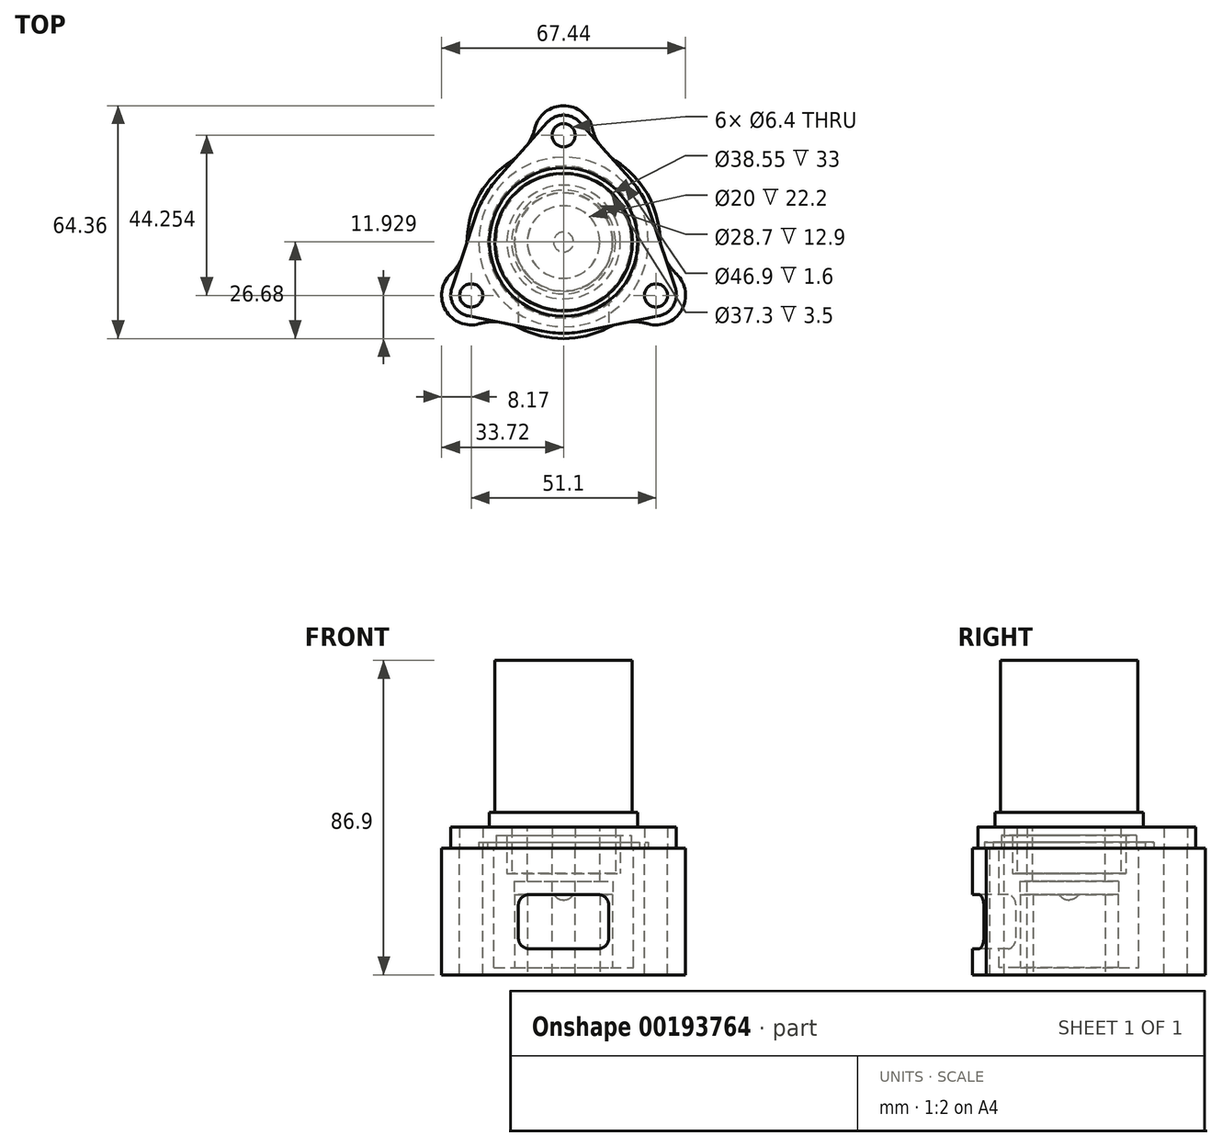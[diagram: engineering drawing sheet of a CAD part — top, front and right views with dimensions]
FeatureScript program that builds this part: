
annotation { "Feature Type Name" : "Feature", "Feature Type Description" : "" }
export const myFeature = defineFeature(function(context is Context, id is Id, definition is map)
    precondition{}
    {
        {
            var Q0;
            Q0=qCreatedBy(makeId("Top.planeOp"),FACE);
            var sketch = newSketch(context, id + "F0", { "sketchPlane" : qUnion([Q0])});
            skCircle(sketch, "E0", {"center": v(0, 29.5) * mm, "radius": 3.2 * mm});
            skCircle(sketch, "E1", {"center": v(25.55, -14.75) * mm, "radius": 3.2 * mm});
            skCircle(sketch, "E2", {"center": v(-25.55, -14.75) * mm, "radius": 3.2 * mm});
            skCircle(sketch, "E3", {"center": v(0, 0) * mm, "radius": 14.35 * mm});
            skLineSegment(sketch, "E4", {"start": v(0, 29.5) * mm, "end": v(25.55, -14.75) * mm, "construction": true});
            skLineSegment(sketch, "E5", {"start": v(-25.55, -14.75) * mm, "end": v(25.55, -14.75) * mm, "construction": true});
            skLineSegment(sketch, "E6", {"start": v(0, 29.5) * mm, "end": v(-25.55, -14.75) * mm, "construction": true});
            skLineSegment(sketch, "E7", {"start": v(-22.39, 12.93) * mm, "end": v(0, 38.1) * mm});
            skLineSegment(sketch, "E8", {"start": v(0, 38.1) * mm, "end": v(22.39, 12.92) * mm});
            skLineSegment(sketch, "E9", {"start": v(22.39, 12.92) * mm, "end": v(33, -19.05) * mm});
            skLineSegment(sketch, "E10", {"start": v(33, -19.05) * mm, "end": v(0, -25.85) * mm});
            skLineSegment(sketch, "E11", {"start": v(0, -25.85) * mm, "end": v(-33, -19.05) * mm});
            skLineSegment(sketch, "E12", {"start": v(-33, -19.05) * mm, "end": v(-22.39, 12.93) * mm});
            skLineSegment(sketch, "E13", {"start": v(0, 38.1) * mm, "end": v(-33, -19.05) * mm, "construction": true});
            skLineSegment(sketch, "E14", {"start": v(0, 38.1) * mm, "end": v(33, -19.05) * mm, "construction": true});
            skLineSegment(sketch, "E15", {"start": v(33, -19.05) * mm, "end": v(-33, -19.05) * mm, "construction": true});
            skLineSegment(sketch, "E16", {"start": v(0, 29.5) * mm, "end": v(0, 38.1) * mm, "construction": true});
            skLineSegment(sketch, "E17", {"start": v(-25.55, -14.75) * mm, "end": v(-33, -19.05) * mm, "construction": true});
            skLineSegment(sketch, "E18", {"start": v(25.55, -14.75) * mm, "end": v(33, -19.05) * mm, "construction": true});
            skLineSegment(sketch, "E19", {"start": v(0, 29.5) * mm, "end": v(0, 0) * mm, "construction": true});
            skLineSegment(sketch, "E20", {"start": v(0, 0) * mm, "end": v(-25.55, -14.75) * mm, "construction": true});
            skLineSegment(sketch, "E21", {"start": v(0, 0) * mm, "end": v(25.55, -14.75) * mm, "construction": true});
            skSolve(sketch);
        }
        {
            var Q0;
            Q0 = qSketchRegion(id + "F0", true);
            extrude(context, id + "F1", {"entities" : qUnion([Q0]), "depth" : 5.9 * mm});
        }
        {
            var Q0;
            Q0=makeQuery(id+"F1.opExtrude","SWEPT_EDGE",EDGE,{"disambiguationData":[OSD([sQuery(id+"F0.wireOp",EDGE,"E11"),sQuery(id+"F0.wireOp",EDGE,"E12")])]});
            var Q1;
            Q1=makeQuery(id+"F1.opExtrude","SWEPT_EDGE",EDGE,{"disambiguationData":[OSD([sQuery(id+"F0.wireOp",EDGE,"E9"),sQuery(id+"F0.wireOp",EDGE,"E10")])]});
            var Q2;
            Q2=makeQuery(id+"F1.opExtrude","SWEPT_EDGE",EDGE,{"disambiguationData":[OSD([sQuery(id+"F0.wireOp",EDGE,"E7"),sQuery(id+"F0.wireOp",EDGE,"E8")])]});
            fillet(context, id + "F2", {"entities" : qUnion([Q0, Q1, Q2]), "radius" : 6 * mm, "tangentPropagation" : true, "allowEdgeOverflow" : false});
        }
        {
            var Q0;
            Q0=makeQuery(id+"F1.opExtrude","SWEPT_EDGE",EDGE,{"disambiguationData":[OSD([sQuery(id+"F0.wireOp",EDGE,"E7"),sQuery(id+"F0.wireOp",EDGE,"E12")])]});
            var Q1;
            Q1=makeQuery(id+"F1.opExtrude","SWEPT_EDGE",EDGE,{"disambiguationData":[OSD([sQuery(id+"F0.wireOp",EDGE,"E8"),sQuery(id+"F0.wireOp",EDGE,"E9")])]});
            var Q2;
            Q2=makeQuery(id+"F1.opExtrude","SWEPT_EDGE",EDGE,{"disambiguationData":[OSD([sQuery(id+"F0.wireOp",EDGE,"E10"),sQuery(id+"F0.wireOp",EDGE,"E11")])]});
            fillet(context, id + "F3", {"entities" : qUnion([Q0, Q1, Q2]), "radius" : 30 * mm, "tangentPropagation" : true, "allowEdgeOverflow" : false});
        }
        {
            var Q0;
            Q0=makeQuery(id+"F1.opExtrude","CAP_FACE",FACE,{"disambiguationData":[OSD([sQuery(id+"F0.wireOp",EDGE,"E0"),sQuery(id+"F0.wireOp",EDGE,"E1"),sQuery(id+"F0.wireOp",EDGE,"E2"),sQuery(id+"F0.wireOp",EDGE,"E3"),sQuery(id+"F0.wireOp",EDGE,"E7"),sQuery(id+"F0.wireOp",EDGE,"E8"),sQuery(id+"F0.wireOp",EDGE,"E9"),sQuery(id+"F0.wireOp",EDGE,"E10"),sQuery(id+"F0.wireOp",EDGE,"E11"),sQuery(id+"F0.wireOp",EDGE,"E12")])],"isStart":true});
            var sketch = newSketch(context, id + "F4", { "sketchPlane" : qUnion([Q0])});
            skCircle(sketch, "E22", {"center": v(0, 0) * mm, "radius": 23.45 * mm});
            skCircle(sketch, "E23", {"center": v(0, 0) * mm, "radius": 21 * mm});
            skSolve(sketch);
        }
        {
            var Q0;
            Q0 = qSketchRegion(id + "F4", true);
            extrude(context, id + "F5", {"entities" : qUnion([Q0]), "operationType" : NewBodyOperationType.REMOVE, "oppositeDirection" : true, "depth" : 1.6 * mm});
        }
        {
            var Q0;
            {var subQ0=sQuery(id+"F0.wireOp",EDGE,"E3");Q0=makeQuery(id+"F5.boolean.opBoolean","SPLIT",FACE,{"disambiguationData":[TD([makeQuery(id+"F1.opExtrude","SWEPT_FACE",FACE,{"disambiguationData":[OSD([subQ0])]})])],"derivedFrom":makeQuery(id+"F1.opExtrude","CAP_FACE",FACE,{"disambiguationData":[OSD([sQuery(id+"F0.wireOp",EDGE,"E0"),sQuery(id+"F0.wireOp",EDGE,"E1"),sQuery(id+"F0.wireOp",EDGE,"E2"),subQ0,sQuery(id+"F0.wireOp",EDGE,"E7"),sQuery(id+"F0.wireOp",EDGE,"E8"),sQuery(id+"F0.wireOp",EDGE,"E9"),sQuery(id+"F0.wireOp",EDGE,"E10"),sQuery(id+"F0.wireOp",EDGE,"E11"),sQuery(id+"F0.wireOp",EDGE,"E12")])],"isStart":true})});}
            var sketch = newSketch(context, id + "F6", { "sketchPlane" : qUnion([Q0])});
            skCircle(sketch, "E24", {"center": v(0, 0) * mm, "radius": 18.65 * mm});
            skCircle(sketch, "E25", {"center": v(0, 0) * mm, "radius": 15.7 * mm});
            skSolve(sketch);
        }
        {
            var Q0;
            Q0 = qSketchRegion(id + "F6", true);
            extrude(context, id + "F7", {"entities" : qUnion([Q0]), "operationType" : NewBodyOperationType.REMOVE, "oppositeDirection" : true, "depth" : 3.5 * mm});
        }
        {
            var Q0;
            {var subQ0=sQuery(id+"F0.wireOp",EDGE,"E3");var subQ1=makeQuery(id+"F1.opExtrude","SWEPT_FACE",FACE,{"disambiguationData":[OSD([subQ0])]});Q0=makeQuery(id+"F7.boolean.opBoolean","SPLIT",FACE,{"disambiguationData":[TD([subQ1])],"derivedFrom":makeQuery(id+"F5.boolean.opBoolean","SPLIT",FACE,{"disambiguationData":[TD([subQ1])],"derivedFrom":makeQuery(id+"F1.opExtrude","CAP_FACE",FACE,{"disambiguationData":[OSD([sQuery(id+"F0.wireOp",EDGE,"E0"),sQuery(id+"F0.wireOp",EDGE,"E1"),sQuery(id+"F0.wireOp",EDGE,"E2"),subQ0,sQuery(id+"F0.wireOp",EDGE,"E7"),sQuery(id+"F0.wireOp",EDGE,"E8"),sQuery(id+"F0.wireOp",EDGE,"E9"),sQuery(id+"F0.wireOp",EDGE,"E10"),sQuery(id+"F0.wireOp",EDGE,"E11"),sQuery(id+"F0.wireOp",EDGE,"E12")])],"isStart":true})})});}
            extrude(context, id + "F8", {"entities" : qUnion([Q0]), "operationType" : NewBodyOperationType.ADD, "depth" : 7 * mm});
        }
        {
            var Q0;
            Q0=qCreatedBy(makeId("Front.planeOp"),FACE);
            var sketch = newSketch(context, id + "F9", { "sketchPlane" : qUnion([Q0])});
            skLineSegment(sketch, "E26", {"start": v(0, 5.9) * mm, "end": v(20.5, 5.9) * mm});
            skLineSegment(sketch, "E27", {"start": v(20.5, 5.9) * mm, "end": v(20.5, 9.9) * mm});
            skLineSegment(sketch, "E28", {"start": v(20.5, 9.9) * mm, "end": v(19, 9.9) * mm});
            skLineSegment(sketch, "E29", {"start": v(19, 9.9) * mm, "end": v(19, 51.9) * mm});
            skLineSegment(sketch, "E30", {"start": v(19, 51.9) * mm, "end": v(0, 51.9) * mm});
            skLineSegment(sketch, "E31", {"start": v(0, 51.9) * mm, "end": v(0, 5.9) * mm});
            skSolve(sketch);
        }
        {
            var Q0;
            Q0 = qSketchRegion(id + "F9", true);
            var Q1;
            Q1=sQuery(id+"F9.wireOp",EDGE,"E31");
            revolve(context, id + "F10", {"operationType" : NewBodyOperationType.ADD, "entities" : qUnion([Q0]), "axis" : qUnion([Q1]), "revolveType" : RevolveType.FULL});
        }
        {
            var Q0;
            Q0=makeQuery(id+"F10.opRevolve","SWEPT_FACE",FACE,{"disambiguationData":[OSD([sQuery(id+"F9.wireOp",EDGE,"E26")])]});
            var sketch = newSketch(context, id + "F11", { "sketchPlane" : qUnion([Q0])});
            skCircle(sketch, "E32", {"center": v(0, 0) * mm, "radius": 10.05 * mm});
            skSolve(sketch);
        }
        {
            var Q0;
            Q0 = qSketchRegion(id + "F11", true);
            var Q1;
            Q1=makeQuery(id+"F8.opExtrude","CAP_FACE",FACE,{"disambiguationData":[OSD([sQuery(id+"F0.wireOp",EDGE,"E0"),sQuery(id+"F0.wireOp",EDGE,"E1"),sQuery(id+"F0.wireOp",EDGE,"E2"),sQuery(id+"F0.wireOp",EDGE,"E3"),sQuery(id+"F0.wireOp",EDGE,"E7"),sQuery(id+"F0.wireOp",EDGE,"E8"),sQuery(id+"F0.wireOp",EDGE,"E9"),sQuery(id+"F0.wireOp",EDGE,"E10"),sQuery(id+"F0.wireOp",EDGE,"E11"),sQuery(id+"F0.wireOp",EDGE,"E12")])],"isStart":false});
            extrude(context, id + "F12", {"entities" : qUnion([Q0]), "endBoundEntityFace" : qUnion([Q1]), "depth" : 18.7 * mm});
        }
        {
            var Q0;
            Q0=makeQuery(id+"F12.opExtrude","CAP_FACE",FACE,{"disambiguationData":[OSD([sQuery(id+"F11.wireOp",EDGE,"E32")])],"isStart":false});
            var sketch = newSketch(context, id + "F13", { "sketchPlane" : qUnion([Q0])});
            skCircle(sketch, "E33", {"center": v(0, 0) * mm, "radius": 13.65 * mm});
            skSolve(sketch);
        }
        {
            var Q0;
            Q0 = qSketchRegion(id + "F13", true);
            extrude(context, id + "F14", {"entities" : qUnion([Q0]), "operationType" : NewBodyOperationType.ADD, "oppositeDirection" : true, "depth" : 3.7 * mm});
        }
        {
            var Q0;
            Q0=qCreatedBy(makeId("Front.planeOp"),FACE);
            var sketch = newSketch(context, id + "F15", { "sketchPlane" : qUnion([Q0])});
            skLineSegment(sketch, "E34", {"start": v(0, -9.1) * mm, "end": v(6.1, -9.1) * mm});
            skLineSegment(sketch, "E35", {"start": v(1.4, -14.3) * mm, "end": v(0, -14.3) * mm});
            skLineSegment(sketch, "E36", {"start": v(0, -14.3) * mm, "end": v(0, -9.1) * mm});
            skLineSegment(sketch, "E37", {"start": v(1.4, -14.3) * mm, "end": v(6.1, -9.1) * mm});
            skSolve(sketch);
        }
        {
            var Q0;
            Q0 = qSketchRegion(id + "F15", true);
            var Q1;
            Q1=sQuery(id+"F15.wireOp",EDGE,"E36");
            revolve(context, id + "F16", {"operationType" : NewBodyOperationType.ADD, "entities" : qUnion([Q0]), "axis" : qUnion([Q1]), "revolveType" : RevolveType.FULL});
        }
        {
            var Q0;
            Q0=makeQuery(id+"F16.opRevolve","SWEPT_EDGE",EDGE,{"disambiguationData":[OSD([sQuery(id+"F15.wireOp",EDGE,"E35"),sQuery(id+"F15.wireOp",EDGE,"E37")])]});
            var Q1;
            Q1=makeQuery(id+"F16.opRevolve","SWEPT_EDGE",EDGE,{"disambiguationData":[OSD([sQuery(id+"F15.wireOp",EDGE,"E34"),sQuery(id+"F15.wireOp",EDGE,"E37")])]});
            fillet(context, id + "F17", {"entities" : qUnion([Q0, Q1]), "radius" : 3 * mm, "tangentPropagation" : true, "allowEdgeOverflow" : false});
        }
        {
            var Q0;
            Q0=qCreatedBy(makeId("Top.planeOp"),FACE);
            var sketch = newSketch(context, id + "F18", { "sketchPlane" : qUnion([Q0])});
            skCircle(sketch, "E38", {"center": v(0, 0) * mm, "radius": 19.28 * mm});
            skArc(sketch, "E39", {"start": v(-18.63, -19.1) * mm, "mid": v(0, -26.68) * mm, "end": v(18.63, -19.1) * mm});
            skCircle(sketch, "E40", {"center": v(0, 29.5) * mm, "radius": 3.2 * mm});
            skCircle(sketch, "E41", {"center": v(-25.55, -14.75) * mm, "radius": 3.2 * mm});
            skCircle(sketch, "E42", {"center": v(25.55, -14.75) * mm, "radius": 3.2 * mm});
            skArc(sketch, "E43", {"start": v(-25.85, -6.58) * mm, "mid": v(-32.63, -18.84) * mm, "end": v(-18.63, -19.1) * mm});
            skArc(sketch, "E44", {"start": v(18.63, -19.1) * mm, "mid": v(32.63, -18.84) * mm, "end": v(25.85, -6.58) * mm});
            skArc(sketch, "E45", {"start": v(7.22, 25.68) * mm, "mid": v(0, 37.67) * mm, "end": v(-7.22, 25.68) * mm});
            skArc(sketch, "E46.trimOffspring", {"start": v(-7.22, 25.68) * mm, "mid": v(-23.1, 13.34) * mm, "end": v(-25.85, -6.58) * mm});
            skArc(sketch, "E47.trimOffspring", {"start": v(25.85, -6.58) * mm, "mid": v(23.1, 13.34) * mm, "end": v(7.22, 25.68) * mm});
            skSolve(sketch);
        }
        {
            var Q0;
            Q0 = qSketchRegion(id + "F18", true);
            extrude(context, id + "F19", {"entities" : qUnion([Q0]), "oppositeDirection" : true, "depth" : 35 * mm});
        }
        {
            var Q0;
            Q0=makeQuery(id+"F19.opExtrude","SWEPT_EDGE",EDGE,{"disambiguationData":[OSD([sQuery(id+"F18.wireOp",EDGE,"E43"),sQuery(id+"F18.wireOp",EDGE,"E46.trimOffspring")])]});
            var Q1;
            Q1=makeQuery(id+"F19.opExtrude","SWEPT_EDGE",EDGE,{"disambiguationData":[OSD([sQuery(id+"F18.wireOp",EDGE,"E45"),sQuery(id+"F18.wireOp",EDGE,"E46.trimOffspring")])]});
            var Q2;
            Q2=makeQuery(id+"F19.opExtrude","SWEPT_EDGE",EDGE,{"disambiguationData":[OSD([sQuery(id+"F18.wireOp",EDGE,"E45"),sQuery(id+"F18.wireOp",EDGE,"E47.trimOffspring")])]});
            var Q3;
            Q3=makeQuery(id+"F19.opExtrude","SWEPT_EDGE",EDGE,{"disambiguationData":[OSD([sQuery(id+"F18.wireOp",EDGE,"E44"),sQuery(id+"F18.wireOp",EDGE,"E47.trimOffspring")])]});
            var Q4;
            Q4=makeQuery(id+"F19.opExtrude","SWEPT_EDGE",EDGE,{"disambiguationData":[OSD([sQuery(id+"F18.wireOp",EDGE,"E39"),sQuery(id+"F18.wireOp",EDGE,"E44")])]});
            var Q5;
            Q5=makeQuery(id+"F19.opExtrude","SWEPT_EDGE",EDGE,{"disambiguationData":[OSD([sQuery(id+"F18.wireOp",EDGE,"E39"),sQuery(id+"F18.wireOp",EDGE,"E43")])]});
            fillet(context, id + "F20", {"entities" : qUnion([Q0, Q1, Q2, Q3, Q4, Q5]), "radius" : 15 * mm, "tangentPropagation" : true, "allowEdgeOverflow" : false});
        }
        {
            var Q0;
            Q0=makeQuery(id+"F19.opExtrude","CAP_FACE",FACE,{"disambiguationData":[OSD([sQuery(id+"F18.wireOp",EDGE,"E38"),sQuery(id+"F18.wireOp",EDGE,"E39"),sQuery(id+"F18.wireOp",EDGE,"E40"),sQuery(id+"F18.wireOp",EDGE,"E41"),sQuery(id+"F18.wireOp",EDGE,"E42"),sQuery(id+"F18.wireOp",EDGE,"E43"),sQuery(id+"F18.wireOp",EDGE,"E44"),sQuery(id+"F18.wireOp",EDGE,"E45"),sQuery(id+"F18.wireOp",EDGE,"E46.trimOffspring"),sQuery(id+"F18.wireOp",EDGE,"E47.trimOffspring")])],"isStart":false});
            var sketch = newSketch(context, id + "F21", { "sketchPlane" : qUnion([Q0])});
            skCircle(sketch, "E48", {"center": v(0, 0) * mm, "radius": 20 * mm});
            skCircle(sketch, "E49", {"center": v(0, 0) * mm, "radius": 10 * mm});
            skSolve(sketch);
        }
        {
            var Q0;
            Q0 = qSketchRegion(id + "F21", true);
            extrude(context, id + "F22", {"entities" : qUnion([Q0]), "operationType" : NewBodyOperationType.ADD, "oppositeDirection" : true, "depth" : 2 * mm});
        }
        {
            var Q0;
            Q0=makeQuery(id+"F22.opExtrude","CAP_FACE",FACE,{"disambiguationData":[OSD([sQuery(id+"F21.wireOp",EDGE,"E48")])],"isStart":false});
            var sketch = newSketch(context, id + "F23", { "sketchPlane" : qUnion([Q0])});
            skCircle(sketch, "E50", {"center": v(0, 0) * mm, "radius": 13.5 * mm});
            skCircle(sketch, "E51", {"center": v(0, 0) * mm, "radius": 10 * mm});
            skSolve(sketch);
        }
        {
            var Q0;
            Q0 = qSketchRegion(id + "F23", true);
            extrude(context, id + "F24", {"entities" : qUnion([Q0]), "operationType" : NewBodyOperationType.ADD, "depth" : (33 - 12.8) * mm});
        }
        {
            var Q0;
            {var subQ0=sQuery(id+"F18.wireOp",EDGE,"E39");var subQ1=sQuery(id+"F18.wireOp",EDGE,"E43");Q0=makeQuery(id+"F20.opFillet","BLEND_VERTEX",VERTEX,{"blendedFrom":[makeQuery(id+"F19.opExtrude","SWEPT_EDGE",EDGE,{"disambiguationData":[OSD([subQ0,subQ1])]}),makeQuery(id+"F19.opExtrude","CAP_FACE",FACE,{"disambiguationData":[OSD([sQuery(id+"F18.wireOp",EDGE,"E38"),subQ0,sQuery(id+"F18.wireOp",EDGE,"E40"),sQuery(id+"F18.wireOp",EDGE,"E41"),sQuery(id+"F18.wireOp",EDGE,"E42"),subQ1,sQuery(id+"F18.wireOp",EDGE,"E44"),sQuery(id+"F18.wireOp",EDGE,"E45"),sQuery(id+"F18.wireOp",EDGE,"E46.trimOffspring"),sQuery(id+"F18.wireOp",EDGE,"E47.trimOffspring")])],"isStart":true}),makeQuery(id+"F19.opExtrude","SWEPT_FACE",FACE,{"disambiguationData":[OSD([subQ0])]})],"blendedInto":[makeQuery(id+"F19.opExtrude","CAP_FACE",FACE,{"disambiguationData":[OSD([sQuery(id+"F18.wireOp",EDGE,"E38"),subQ0,sQuery(id+"F18.wireOp",EDGE,"E40"),sQuery(id+"F18.wireOp",EDGE,"E41"),sQuery(id+"F18.wireOp",EDGE,"E42"),subQ1,sQuery(id+"F18.wireOp",EDGE,"E44"),sQuery(id+"F18.wireOp",EDGE,"E45"),sQuery(id+"F18.wireOp",EDGE,"E46.trimOffspring"),sQuery(id+"F18.wireOp",EDGE,"E47.trimOffspring")])],"isStart":true}),makeQuery(id+"F19.opExtrude","SWEPT_FACE",FACE,{"disambiguationData":[OSD([subQ0])]})]});}
            var Q1;
            {var subQ0=sQuery(id+"F18.wireOp",EDGE,"E39");var subQ1=sQuery(id+"F18.wireOp",EDGE,"E43");Q1=makeQuery(id+"F20.opFillet","BLEND_VERTEX",VERTEX,{"blendedFrom":[makeQuery(id+"F19.opExtrude","SWEPT_EDGE",EDGE,{"disambiguationData":[OSD([subQ0,subQ1])]}),makeQuery(id+"F19.opExtrude","CAP_FACE",FACE,{"disambiguationData":[OSD([sQuery(id+"F18.wireOp",EDGE,"E38"),subQ0,sQuery(id+"F18.wireOp",EDGE,"E40"),sQuery(id+"F18.wireOp",EDGE,"E41"),sQuery(id+"F18.wireOp",EDGE,"E42"),subQ1,sQuery(id+"F18.wireOp",EDGE,"E44"),sQuery(id+"F18.wireOp",EDGE,"E45"),sQuery(id+"F18.wireOp",EDGE,"E46.trimOffspring"),sQuery(id+"F18.wireOp",EDGE,"E47.trimOffspring")])],"isStart":false}),makeQuery(id+"F19.opExtrude","SWEPT_FACE",FACE,{"disambiguationData":[OSD([subQ0])]})],"blendedInto":[makeQuery(id+"F19.opExtrude","CAP_FACE",FACE,{"disambiguationData":[OSD([sQuery(id+"F18.wireOp",EDGE,"E38"),subQ0,sQuery(id+"F18.wireOp",EDGE,"E40"),sQuery(id+"F18.wireOp",EDGE,"E41"),sQuery(id+"F18.wireOp",EDGE,"E42"),subQ1,sQuery(id+"F18.wireOp",EDGE,"E44"),sQuery(id+"F18.wireOp",EDGE,"E45"),sQuery(id+"F18.wireOp",EDGE,"E46.trimOffspring"),sQuery(id+"F18.wireOp",EDGE,"E47.trimOffspring")])],"isStart":false}),makeQuery(id+"F19.opExtrude","SWEPT_FACE",FACE,{"disambiguationData":[OSD([subQ0])]})]});}
            var Q2;
            {var subQ0=sQuery(id+"F18.wireOp",EDGE,"E39");var subQ1=sQuery(id+"F18.wireOp",EDGE,"E44");Q2=makeQuery(id+"F20.opFillet","BLEND_VERTEX",VERTEX,{"blendedFrom":[makeQuery(id+"F19.opExtrude","SWEPT_EDGE",EDGE,{"disambiguationData":[OSD([subQ0,subQ1])]}),makeQuery(id+"F19.opExtrude","CAP_FACE",FACE,{"disambiguationData":[OSD([sQuery(id+"F18.wireOp",EDGE,"E38"),subQ0,sQuery(id+"F18.wireOp",EDGE,"E40"),sQuery(id+"F18.wireOp",EDGE,"E41"),sQuery(id+"F18.wireOp",EDGE,"E42"),sQuery(id+"F18.wireOp",EDGE,"E43"),subQ1,sQuery(id+"F18.wireOp",EDGE,"E45"),sQuery(id+"F18.wireOp",EDGE,"E46.trimOffspring"),sQuery(id+"F18.wireOp",EDGE,"E47.trimOffspring")])],"isStart":false}),makeQuery(id+"F19.opExtrude","SWEPT_FACE",FACE,{"disambiguationData":[OSD([subQ0])]})],"blendedInto":[makeQuery(id+"F19.opExtrude","CAP_FACE",FACE,{"disambiguationData":[OSD([sQuery(id+"F18.wireOp",EDGE,"E38"),subQ0,sQuery(id+"F18.wireOp",EDGE,"E40"),sQuery(id+"F18.wireOp",EDGE,"E41"),sQuery(id+"F18.wireOp",EDGE,"E42"),sQuery(id+"F18.wireOp",EDGE,"E43"),subQ1,sQuery(id+"F18.wireOp",EDGE,"E45"),sQuery(id+"F18.wireOp",EDGE,"E46.trimOffspring"),sQuery(id+"F18.wireOp",EDGE,"E47.trimOffspring")])],"isStart":false}),makeQuery(id+"F19.opExtrude","SWEPT_FACE",FACE,{"disambiguationData":[OSD([subQ0])]})]});}
            cPlane(context, id + "F25", {"entities" : qUnion([Q0, Q1, Q2]), "cplaneType" : CPlaneType.THREE_POINT, "offset" : 25 * mm, "width" : 150 * mm, "height" : 150 * mm});
        }
        {
            var Q0;
            Q0=qCreatedBy(id+"F25.planeOp",FACE);
            var sketch = newSketch(context, id + "F26", { "sketchPlane" : qUnion([Q0])});
            skLineSegment(sketch, "E52.bottom", {"start": v(12.5, -12.8) * mm, "end": v(-12.5, -12.8) * mm});
            skLineSegment(sketch, "E52.top", {"start": v(12.5, -27.8) * mm, "end": v(-12.5, -27.8) * mm});
            skLineSegment(sketch, "E52.left", {"start": v(12.5, -12.8) * mm, "end": v(12.5, -27.8) * mm});
            skLineSegment(sketch, "E52.right", {"start": v(-12.5, -12.8) * mm, "end": v(-12.5, -27.8) * mm});
            skPoint(sketch, "E53", {"position": v(0, -12.8) * mm});
            skSolve(sketch);
        }
        {
            var Q0;
            Q0 = qSketchRegion(id + "F26", true);
            extrude(context, id + "F27", {"entities" : qUnion([Q0]), "operationType" : NewBodyOperationType.REMOVE, "depth" : 10 * mm, "hasSecondDirection" : true, "secondDirectionOppositeDirection" : true, "secondDirectionDepth" : 5 * mm});
        }
        {
            var Q0;
            Q0=makeQuery(id+"F27.boolean.opBoolean","COPY",EDGE,{"derivedFrom":makeQuery(id+"F27.opExtrude","SWEPT_EDGE",EDGE,{"disambiguationData":[OSD([sQuery(id+"F26.wireOp",EDGE,"E52.bottom"),sQuery(id+"F26.wireOp",EDGE,"E52.left")])]})});
            var Q1;
            Q1=makeQuery(id+"F27.boolean.opBoolean","COPY",EDGE,{"derivedFrom":makeQuery(id+"F27.opExtrude","SWEPT_EDGE",EDGE,{"disambiguationData":[OSD([sQuery(id+"F26.wireOp",EDGE,"E52.top"),sQuery(id+"F26.wireOp",EDGE,"E52.left")])]})});
            var Q2;
            Q2=makeQuery(id+"F27.boolean.opBoolean","COPY",EDGE,{"derivedFrom":makeQuery(id+"F27.opExtrude","SWEPT_EDGE",EDGE,{"disambiguationData":[OSD([sQuery(id+"F26.wireOp",EDGE,"E52.top"),sQuery(id+"F26.wireOp",EDGE,"E52.right")])]})});
            var Q3;
            Q3=makeQuery(id+"F27.boolean.opBoolean","COPY",EDGE,{"derivedFrom":makeQuery(id+"F27.opExtrude","SWEPT_EDGE",EDGE,{"disambiguationData":[OSD([sQuery(id+"F26.wireOp",EDGE,"E52.bottom"),sQuery(id+"F26.wireOp",EDGE,"E52.right")])]})});
            fillet(context, id + "F28", {"entities" : qUnion([Q0, Q1, Q2, Q3]), "radius" : 3 * mm, "tangentPropagation" : true, "allowEdgeOverflow" : false});
        }
    });
